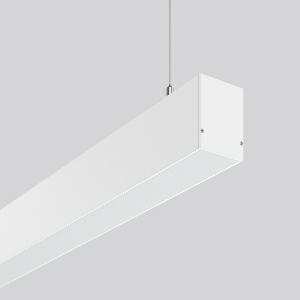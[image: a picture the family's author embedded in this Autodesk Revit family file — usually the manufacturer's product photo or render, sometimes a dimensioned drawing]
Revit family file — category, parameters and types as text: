
# Revit family: less_is_more_50_312317_002_1_76_86b3
name_source: partatom
category: Lighting Fixtures
units: mm (PartAtom-declared; Revit-internal decimal feet)

## family parameters
Cut with Voids When Loaded = No
Host = Face
Light Source = No
Part Type = Normal
Room Calculation Point = No
Round Connector Dimension = Use Diameter
Shared = No

## types (1)
- LESS IS MORE 50 (1 x LED Modul 840, 4000 lm, 4000)
    Apparent Load = 34 VA
    CIE Flux Codes = 49 80 96 63 100
    Color Rendering = 80
    Color Temperature = 4000
    Default Elevation = 1800 mm
    Description = Series: LESS IS MORE 50
Linear pendant luminaire for aesthetically sophisticated lighting. Housing: extruded aluminium profile, powder-coated. End cap aluminium powder-coated. Canopy made of aluminium, powder-coated. Diffuser made of non-yellowing plastic (PMMA), opal. Direct 65%, indirect 35% light emission. Suitable for pendant. 2-point steel cable suspension freely positionable and infinitely height-adjustable. Special lengths available on request. LED unit with integrated converter interchangeable and removable. Suitable for through-wiring. With sensors or as a safety luminaire on request. 
Colour: traffic white, matt (RAL 9016)
Length: 847 mm
Width: 57 mm
Height: 75 mm
Suspension length: 2000 mm
Lamp: LED
Socket: without socket
Colour temperature: 4000K
Colour rendering index (CRI): 80
Light source: LED
Socket lamp2: Without base
Colour temperature: 4000K
System power: 34 W
Rated luminous flux: 4000 lm
Luminous efficiency: 118 lm/W
Control gear: Converter, dimmable, DALI
Control gear: Converter, dimmable, DALI
Protection class: I
Type of protection: IP 20
    Height = 75 mm
    Lamp = 1 x LED Modul 840
    Lamp Light Flux = 4000 lm
    Lamp count = 1
    Length = 847 mm
    Lifetime = 50000 h
    Luminous efficacy = 118 lm/W
    Manufacturer = RZB
    ModVariant = No
    Model = 312317.002.1.76
    Mounting Place = Ceiling
    Mounting Type = Pendant
    Number of Poles = 1
    OnlyDefault = Yes
    Power Factor = 1
    Product Name = LESS IS MORE 50
    Product group = Pendant LED linear luminaires
    ProductGroupID = 907
    Protection Class = Protection class I
    Protection Degree = IP 20
    RLX_Detail_Level = 1
    RLX_Emergency_Light_Flux = 0 lm
    RLX_Emergency_Type = 0
    RLX_Emergency_Type_DB = No
    RlxData = <blob elided: 31589 chars, md5=71916e58>
    Socket = socket
    Standby Power = 0 W
    System Light Flux = 4000 lm
    System Power = 34 W
    Type Comments = Product without accessories
    Type Image = 312318.002.jpg
    URL = http://relux.com
    VarID = ---
    Voltage = 230 V
    Voltage Range = 220-240 V
    Weight = 0.00 kg
    Width = 57 mm

## geometry (parser evidence)
native form markers: Blend x4, Sweep x13
no freeform markers — native parametric forms only
